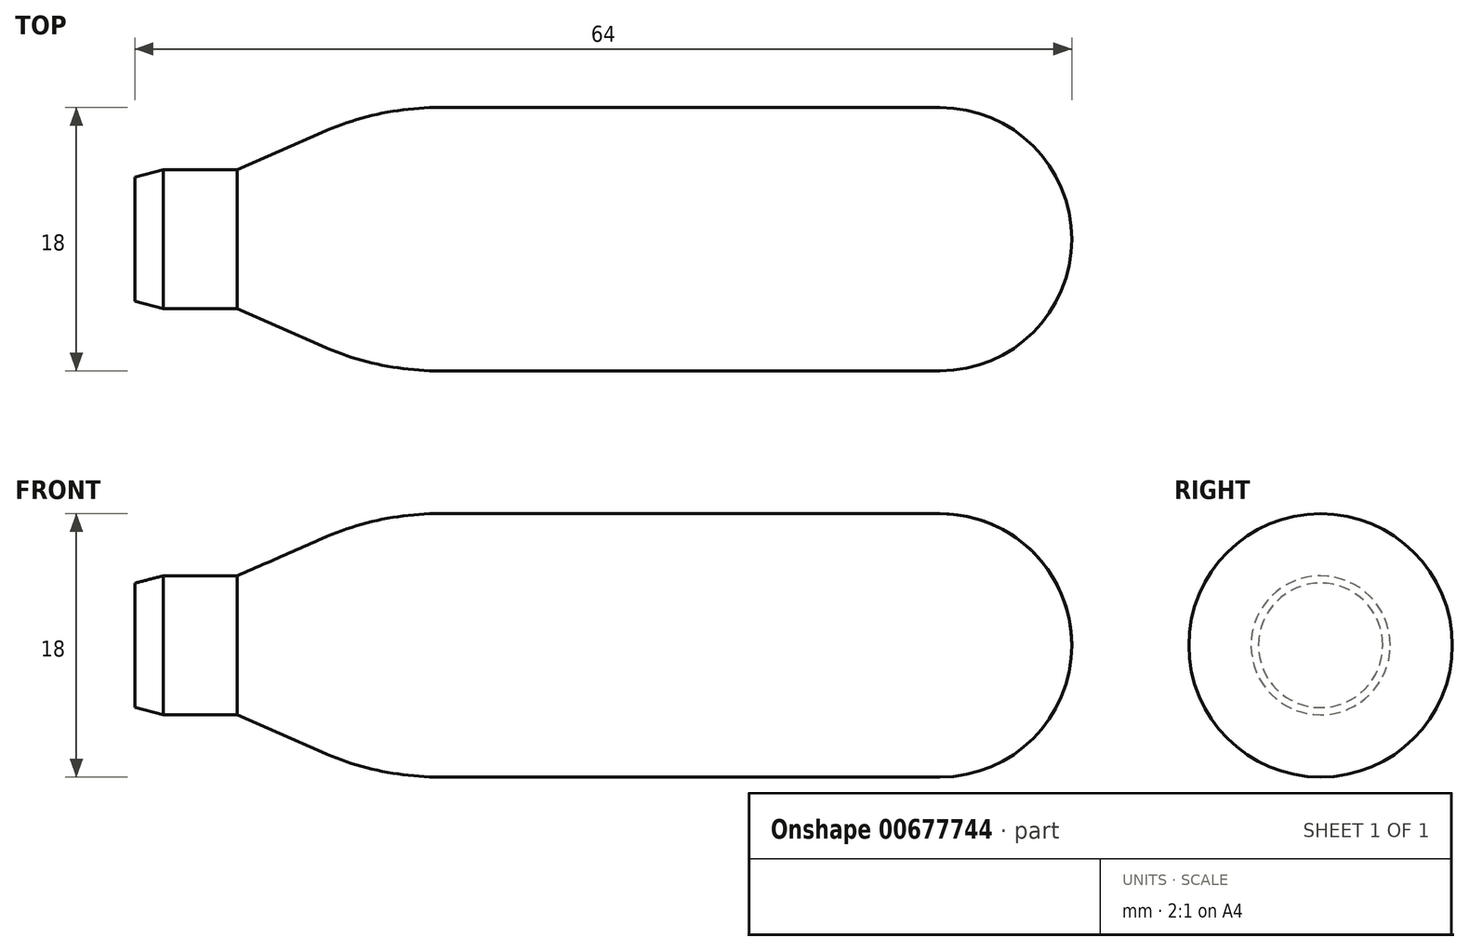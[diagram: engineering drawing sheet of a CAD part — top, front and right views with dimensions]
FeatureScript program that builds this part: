
annotation { "Feature Type Name" : "Feature", "Feature Type Description" : "" }
export const myFeature = defineFeature(function(context is Context, id is Id, definition is map)
    precondition{}
    {
        {
            var Q0;
            Q0=qCreatedBy(makeId("Front.planeOp"),FACE);
            var sketch = newSketch(context, id + "F0", { "sketchPlane" : qUnion([Q0])});
            skLineSegment(sketch, "E0", {"start": v(0, 0) * mm, "end": v(0, 4.25) * mm});
            skLineSegment(sketch, "E1", {"start": v(0, 4.25) * mm, "end": v(1.94, 4.75) * mm});
            skLineSegment(sketch, "E2", {"start": v(1.94, 4.75) * mm, "end": v(7, 4.75) * mm});
            skLineSegment(sketch, "E3", {"start": v(0, 0) * mm, "end": v(64, 0) * mm});
            skLineSegment(sketch, "E4", {"start": v(7, 4.75) * mm, "end": v(12.78, 7.3) * mm});
            skLineSegment(sketch, "E5", {"start": v(20.85, 9) * mm, "end": v(64, 9) * mm});
            skLineSegment(sketch, "E6", {"start": v(64, 0) * mm, "end": v(64, 0) * mm});
            skPoint(sketch, "E7.visualSharp", {"position": v(16.64, 9) * mm});
            skArc(sketch, "E7.filletArc", {"start": v(20.85, 9) * mm, "mid": v(16.73, 8.57) * mm, "end": v(12.78, 7.3) * mm});
            skLineSegment(sketch, "E8", {"start": v(64, 0) * mm, "end": v(64, 9) * mm});
            skSolve(sketch);
        }
        {
            var Q0;
            Q0=makeQuery(id+"F0.imprint","IMPRINT",FACE,{"disambiguationData":[TD([[makeQuery(id+"F0.imprint","IMPRINT",EDGE,{"derivedFrom":sQuery(id+"F0.wireOp",EDGE,"E0")}),-1.0]])]});
            var Q1;
            Q1=sQuery(id+"F0.wireOp",EDGE,"E3");
            revolve(context, id + "F1", {"entities" : qUnion([Q0]), "axis" : qUnion([Q1]), "revolveType" : RevolveType.FULL});
        }
        {
            var Q0;
            Q0=makeQuery(id+"F1.opRevolve","SWEPT_EDGE",EDGE,{"disambiguationData":[OSD([sQuery(id+"F0.wireOp",EDGE,"E5"),sQuery(id+"F0.wireOp",EDGE,"E8")])]});
            fillet(context, id + "F2", {"entities" : qUnion([Q0]), "radius" : 9 * mm, "tangentPropagation" : true, "allowEdgeOverflow" : false});
        }
    });
